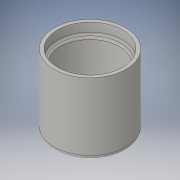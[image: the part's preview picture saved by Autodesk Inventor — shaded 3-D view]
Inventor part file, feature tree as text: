
AUTODESK INVENTOR PART (.ipt)
format: ipt  version: 2016 (Build 200138000, 138)  size: 147,456 bytes
history: native  units: in
note: dims shown in document units (in); Inventor stores cm internally (conversion verified against a paired STEP export)
features: fillet x4, extrude x2, sketch x2, shell x1
ambient origin geometry x8: Origin, YZ Plane, XZ Plane, XY Plane, X Axis, Y Axis, Z Axis, Center Point
bodies: Solid1 (feature_tree)
feature tree (9):
  extrude  "Extrusion1"  Depth=1.0in TaperAngle=0.0deg
  shell  "Shell1"  Thickness=0.09in
  extrude  "Extrusion2"  Depth=0.0312in TaperAngle=0.0deg
  fillet  "Fillet1"  Radius=0.0625in
  fillet  "Fillet2"  Radius=0.0625in
  fillet  "Fillet3"  Radius=0.0312in
  fillet  "Fillet4"  Radius=0.0312in
  sketch  "Sketch1"  dims[d1=1.0in d2=1.0in d3=0.0in d4=0.09in]
  sketch  "Sketch2"  dims[d5=0.907in d6=0.15in d7=0.0in d8=0.0625in d9=0.0625in d10=0.0312in d11=0.0312in]
